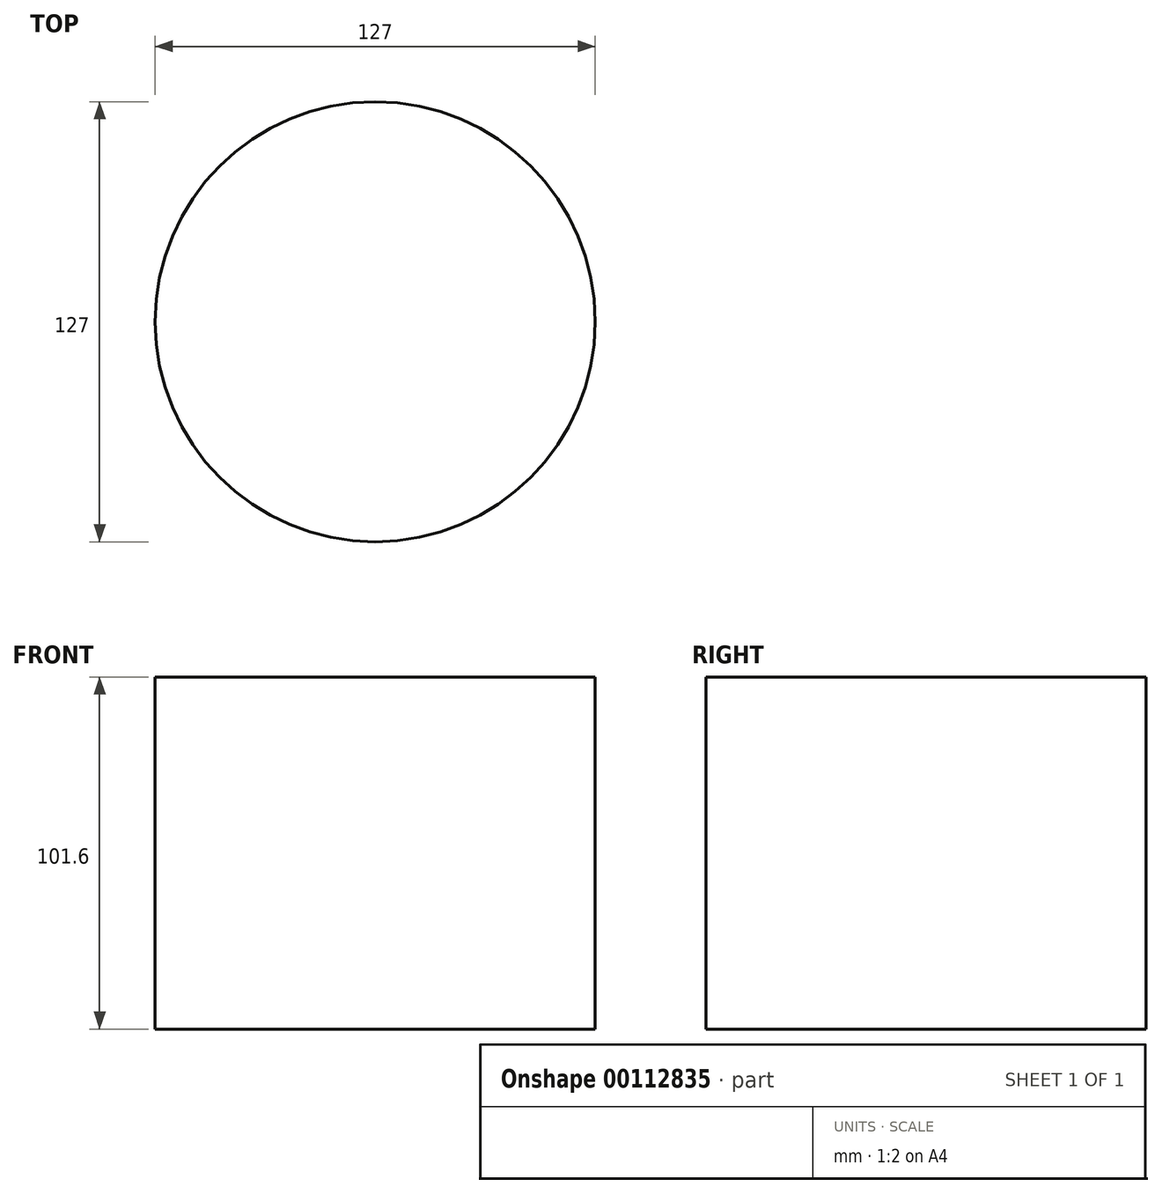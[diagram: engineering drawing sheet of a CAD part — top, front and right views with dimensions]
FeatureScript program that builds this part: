
annotation { "Feature Type Name" : "Feature", "Feature Type Description" : "" }
export const myFeature = defineFeature(function(context is Context, id is Id, definition is map)
    precondition{}
    {
        {
            var Q0;
            Q0=qCreatedBy(makeId("Top.planeOp"),FACE);
            var sketch = newSketch(context, id + "F0", { "sketchPlane" : qUnion([Q0])});
            skCircle(sketch, "E0", {"center": v(0, 0) * mm, "radius": 63.5 * mm});
            skSolve(sketch);
        }
        {
            var Q0;
            Q0=makeQuery(id+"F0.imprint","IMPRINT",FACE,{"disambiguationData":[TD([[makeQuery(id+"F0.imprint","IMPRINT",EDGE,{"derivedFrom":sQuery(id+"F0.wireOp",EDGE,"E0")}),1.0]])]});
            extrude(context, id + "F1", {"entities" : qUnion([Q0]), "depth" : 101.6 * mm});
        }
    });
